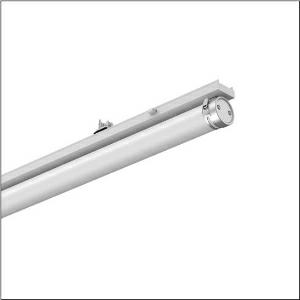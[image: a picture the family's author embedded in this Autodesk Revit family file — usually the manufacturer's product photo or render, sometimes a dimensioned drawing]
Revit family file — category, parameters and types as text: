
# Revit family: monsun_r__31_tube_51ft10mn4a0atr1_8ef5
name_source: partatom
category: Lighting Fixtures
units: mm (PartAtom-declared; Revit-internal decimal feet)

## family parameters
Cut with Voids When Loaded = No
Host = Face
Light Source = No
Part Type = Normal
Room Calculation Point = No
Round Connector Dimension = Use Diameter
Shared = No

## types (1)
- --- (1 x LED, 10000 lm, 58 W, 4000K)
    Apparent Load = 58 VA
    CIE Flux Codes = 42 71 90 91 100
    Color Rendering = 80
    Color Temperature = 4000K
    Default Elevation = 1800 mm
    Description = Monsun® 31 Tube, tubular luminaire, primary optical cover: diffuser, of PMMA, light emission: direct distribution, primary light characteristic: symmetric, LED, rated luminous flux: 10.000lm, luminous efficacy: 172lm/W, light colour: 840, colour temperature: 4000K, control gear: ON/OFF Multilumen, with with 1 terminal, 3-pole, max. 2.5mm², mains connection: 220..240V, AC, 50/60Hz, rated input power: 58W, housing, cylindrical, of PMMA, semi-transparent, matt white, with luminaire and ceiling fastening, V4A, mounting with brackets of stainless steel, length: 1.495mm, diameter: 75mm, end cap, of stainless steel (V4A), protection rating (complete): IP20, protection rating (lamp compartment): IP67/69K, insulation class (complete): insulation class I (protective earthing), certification: CE, UKCA, impact resistance: IK07, permissible operating ambient temperature: -20..+40°C, corresponds to IFS (International Featured Standards) requirements for safety and quality in the food industry, contact your sales advisor before using the luminaires in applications with unclear chemical exposure, large temperature fluctuations or condensation-forming humidity, packaging unit: 1 piece
    Height = 118 mm
    Lamp = 1 x LED
    Lamp Light Flux = 10000 lm
    Lamp Power = 58 W
    Lamp count = 1
    Length = 1495 mm
    Luminous efficacy = 172 lm/W
    Manufacturer = Siteco
    ModVariant = No
    Model = 51FT10MN4A0ATR1
    Mounting Place = Ceiling
    Mounting Type = Pendant
    Number of Poles = 1
    OnlyDefault = Yes
    Power Factor = 1
    Product Name = Monsun® 31 Tube
    Product group = tubular luminaire
    ProductGroupID = 906
    Protection Class = Protection class I
    Protection Degree = IP 20
    RLX_Detail_Level = 1
    RLX_Emergency_Light_Flux = 0 lm
    RLX_Emergency_Type = 0
    RLX_Emergency_Type_DB = No
    RlxData = <blob elided: 32317 chars, md5=9cad82d7>
    Socket = socket
    Standby Power = 0 W
    System Light Flux = 10000 lm
    System Power = 58 W
    Type Comments = factory setting: luminous flux: 100 % | (OFF | OFF | OFF | OFF) | 350 mA
    Type Image = l_1007227.jpg
    URL = http://relux.com
    VarID = @adj_164857
    Voltage = 0 V
    Weight = 0.00 kg
    Width = 75 mm

## geometry (parser evidence)
native form markers: Blend x4, Sweep x11
no freeform markers — native parametric forms only
